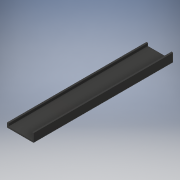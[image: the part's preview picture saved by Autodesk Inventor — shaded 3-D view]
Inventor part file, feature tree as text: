
AUTODESK INVENTOR PART (.ipt)
format: ipt  version: 2019.4 (Build 234330000, 330)  size: 103,936 bytes
history: native  units: mm
features: other x1, extrude x1, sketch x1
ambient origin geometry x8: Origin, YZ Plane, XZ Plane, XY Plane, X Axis, Y Axis, Z Axis, Center Point
bodies: Body1 (feature_tree)
feature tree (3):
  other  "Sólido1"
  extrude  "Extrusão1"  Depth=10.0mm
  sketch  "Esboço1"  dims[d0=190.0mm d1=10.0mm d2=60.0mm d3=10.0mm d4=10.0mm d5=30.0mm d6=1000.0mm d7=0.0mm]
